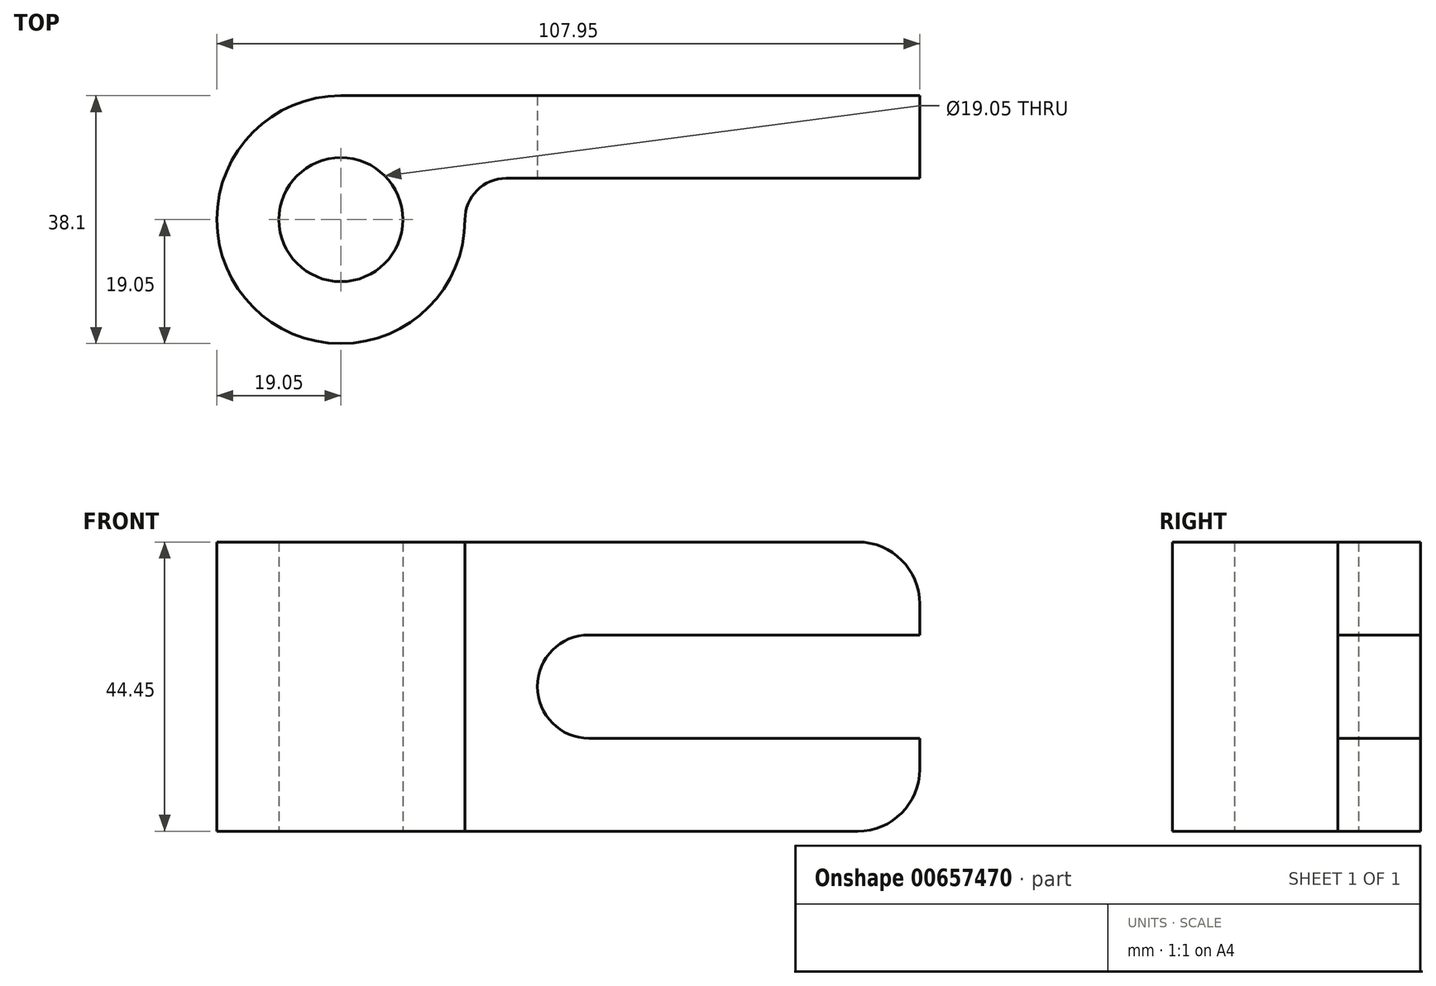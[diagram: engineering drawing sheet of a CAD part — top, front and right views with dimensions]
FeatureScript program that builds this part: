
annotation { "Feature Type Name" : "Feature", "Feature Type Description" : "" }
export const myFeature = defineFeature(function(context is Context, id is Id, definition is map)
    precondition{}
    {
        {
            var Q0;
            Q0=qCreatedBy(makeId("Top.planeOp"),FACE);
            var sketch = newSketch(context, id + "F0", { "sketchPlane" : qUnion([Q0])});
            skLineSegment(sketch, "E0.bottom", {"start": v(0, 0) * mm, "end": v(0, 12.7) * mm});
            skLineSegment(sketch, "E0.left", {"start": v(0, 0) * mm, "end": v(-63.5, 0) * mm});
            skLineSegment(sketch, "E0.right", {"start": v(0, 12.7) * mm, "end": v(-88.9, 12.7) * mm});
            skArc(sketch, "E1", {"start": v(-88.9, 12.7) * mm, "mid": v(-102.37, -19.82) * mm, "end": v(-69.85, -6.35) * mm});
            skCircle(sketch, "E2", {"center": v(-88.9, -6.35) * mm, "radius": 9.53 * mm});
            skPoint(sketch, "E3.visualSharp", {"position": v(-70.94, 0) * mm});
            skArc(sketch, "E3.filletArc", {"start": v(-63.5, 0) * mm, "mid": v(-68, -1.86) * mm, "end": v(-69.85, -6.35) * mm});
            skSolve(sketch);
        }
        {
            var Q0;
            Q0 = qSketchRegion(id + "F0", true);
            extrude(context, id + "F1", {"entities" : qUnion([Q0]), "depth" : 44.45 * mm, "offsetDistance" : 25.4 * mm});
        }
        {
            var Q0;
            Q0=makeQuery(id+"F1.opExtrude","SWEPT_FACE",FACE,{"disambiguationData":[OSD([sQuery(id+"F0.wireOp",EDGE,"E0.left")])]});
            var sketch = newSketch(context, id + "F2", { "sketchPlane" : qUnion([Q0])});
            skLineSegment(sketch, "E4.bottom", {"start": v(-9.52, 44.45) * mm, "end": v(-50.8, 44.45) * mm});
            skLineSegment(sketch, "E4.top", {"start": v(0, 30.16) * mm, "end": v(-50.8, 30.16) * mm});
            skLineSegment(sketch, "E4.left", {"start": v(0, 34.93) * mm, "end": v(0, 30.16) * mm});
            skLineSegment(sketch, "E5.bottom", {"start": v(-9.52, 0) * mm, "end": v(-50.8, 0) * mm});
            skLineSegment(sketch, "E5.top", {"start": v(0, 14.29) * mm, "end": v(-50.8, 14.29) * mm});
            skLineSegment(sketch, "E5.left", {"start": v(0, 9.53) * mm, "end": v(0, 14.29) * mm});
            skArc(sketch, "E6", {"start": v(-50.8, 30.16) * mm, "mid": v(-58.74, 22.22) * mm, "end": v(-50.8, 14.29) * mm});
            skPoint(sketch, "E7.visualSharp", {"position": v(0, 0) * mm});
            skArc(sketch, "E7.filletArc", {"start": v(-9.52, 0) * mm, "mid": v(-2.79, 2.79) * mm, "end": v(0, 9.53) * mm});
            skPoint(sketch, "E8.visualSharp", {"position": v(0, 44.45) * mm});
            skArc(sketch, "E8.filletArc", {"start": v(0, 34.93) * mm, "mid": v(-2.79, 41.66) * mm, "end": v(-9.53, 44.45) * mm});
            skSolve(sketch);
        }
        {
            var Q0;
            Q0 = qSketchRegion(id + "F2", true);
            var Q1;
            {var subQ0=sQuery(id+"F2.wireOp",EDGE,"E4.top");Q1=makeQuery(id+"F2.imprint","IMPRINT",FACE,{"disambiguationData":[TD([[makeQuery(id+"F2.imprint","IMPRINT",EDGE,{"derivedFrom":subQ0}),1.0]])]});}
            var Q2;
            {var subQ0=sQuery(id+"F2.wireOp",EDGE,"E7.filletArc");Q2=makeQuery(id+"F2.imprint","IMPRINT",FACE,{"disambiguationData":[TD([[makeQuery(id+"F2.imprint","IMPRINT",EDGE,{"derivedFrom":subQ0}),-1.0]])]});}
            var Q3;
            {var subQ0=sQuery(id+"F2.wireOp",EDGE,"E8.filletArc");Q3=makeQuery(id+"F2.imprint","IMPRINT",FACE,{"disambiguationData":[TD([[makeQuery(id+"F2.imprint","IMPRINT",EDGE,{"derivedFrom":subQ0}),-1.0]])]});}
            extrude(context, id + "F3", {"entities" : qUnion([Q0, Q1, Q2, Q3]), "operationType" : NewBodyOperationType.REMOVE, "oppositeDirection" : true, "depth" : 12.7 * mm, "offsetDistance" : 25.4 * mm});
        }
    });
